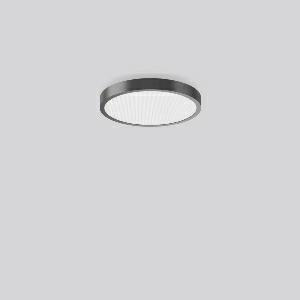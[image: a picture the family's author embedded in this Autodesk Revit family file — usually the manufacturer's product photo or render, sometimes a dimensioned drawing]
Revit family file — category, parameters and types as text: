
# Revit family: triona_round_a_312424_0031_2_730_25d4
name_source: partatom
category: Lighting Fixtures
units: mm (PartAtom-declared; Revit-internal decimal feet)

## family parameters
Cut with Voids When Loaded = No
Host = Face
Light Source = No
Part Type = Normal
Room Calculation Point = No
Round Connector Dimension = Use Diameter
Shared = No

## types (1)
- TuneableWhite 846 (1 x LED Modul 846, 3250 lm, 4600)
    Apparent Load = 38 VA
    CIE Flux Codes = 58 87 97 82 100
    Color Rendering = 80
    Color Temperature = 4600
    Default Elevation = 1800 mm
    Description = Series: TRIONA round
Decorative round LED surface-mounted luminaire. Flat, seamless frame: aluminium extrusion profile, powder coated. Cover made of sheet steel, powder-coated. Direct light emission through a diffuser plastic opal/prismatic. Indirect light emission through a flush diffuser made of satin-finish plastic. Lightguide and diffuser made of non-yellowing plastic (PMMA). Lateral light emission (RZB SIDELITE technology) for above-average homogeneous light distribution. Direct 70%, indirect 30% light emission. Tunable white versions, dynamically adjustable from 2700 K to 6500 K. Suitable for Ceiling mounting, Wall (surface). Tool-free mounting via bayonet connection. Electronic ballast included. Very easy installation thanks to Plug+Play connection. With Casambi smart+free Bluetooth control for wireless network and operation using Android / iOS devices, free app available for download. Perfect for office areas (RUG < 19) and environments with computer screens in accordance with EN 12464-1. Ideal for use as part of the Human Centric Lighting concept in connection with RZB light management systems. 
Colour: anthracite metallic (DB703)
Diameter: 461 mm
Height: 88 mm
Lamp: LED
Socket: without socket
Colour temperature: 2700K - 6500K
Colour rendering index (CRI): 80
System power: 38 W
Rated luminous flux: 3250 lm
Luminous efficiency: 86 lm/W
System power 2: 39 W
Rated luminous flux 2: 3100 lm
Luminous efficiency 2: 79 lm/W
System power 3: 39 W
Rated luminous flux 3: 3150 lm
Luminous efficiency 3: 81 lm/W
Control gear: Dimmable Bluetooth converter
Protection class: I
Type of protection: IP 20
    Height = 88 mm
    Lamp = 1 x LED Modul 846
    Lamp Light Flux = 3250 lm
    Lamp count = 1
    Length = 461 mm
    Lifetime = 50000 h
    Luminous efficacy = 86 lm/W
    Manufacturer = RZB
    ModVariant = No
    Model = 312424.0031.2.730
    Mounting Place = Ceiling
    Mounting Type = Surface mounted
    Number of Poles = 1
    OnlyDefault = Yes
    Power Factor = 1
    Product Name = TRIONA round A
    Product group = Surface mounted modular luminaires
    ProductGroupID = 306
    Protection Class = Protection class I
    Protection Degree = IP 20
    RLX_Detail_Level = 1
    RLX_Emergency_Light_Flux = 0 lm
    RLX_Emergency_Type = 0
    RLX_Emergency_Type_DB = No
    RlxData = <blob elided: 40853 chars, md5=08483102>
    Socket = socket
    Standby Power = 0 W
    System Light Flux = 3250 lm
    System Power = 38 W
    Type Comments = TuneableWhite 846
    Type Image = 312424.0031.jpg
    URL = http://relux.com
    VarID = tuneablewhite_846
    Voltage = 230 V
    Voltage Range = 220-240 V
    Weight = 0.00 kg
    Width = 0 mm  [stored 0 ft]

note: [stored X ft] marks values corroborated as IEEE doubles in the binary element streams (Revit-internal decimal feet)

## geometry (parser evidence)
native form markers: Blend x4, Sweep x15
no freeform markers — native parametric forms only
